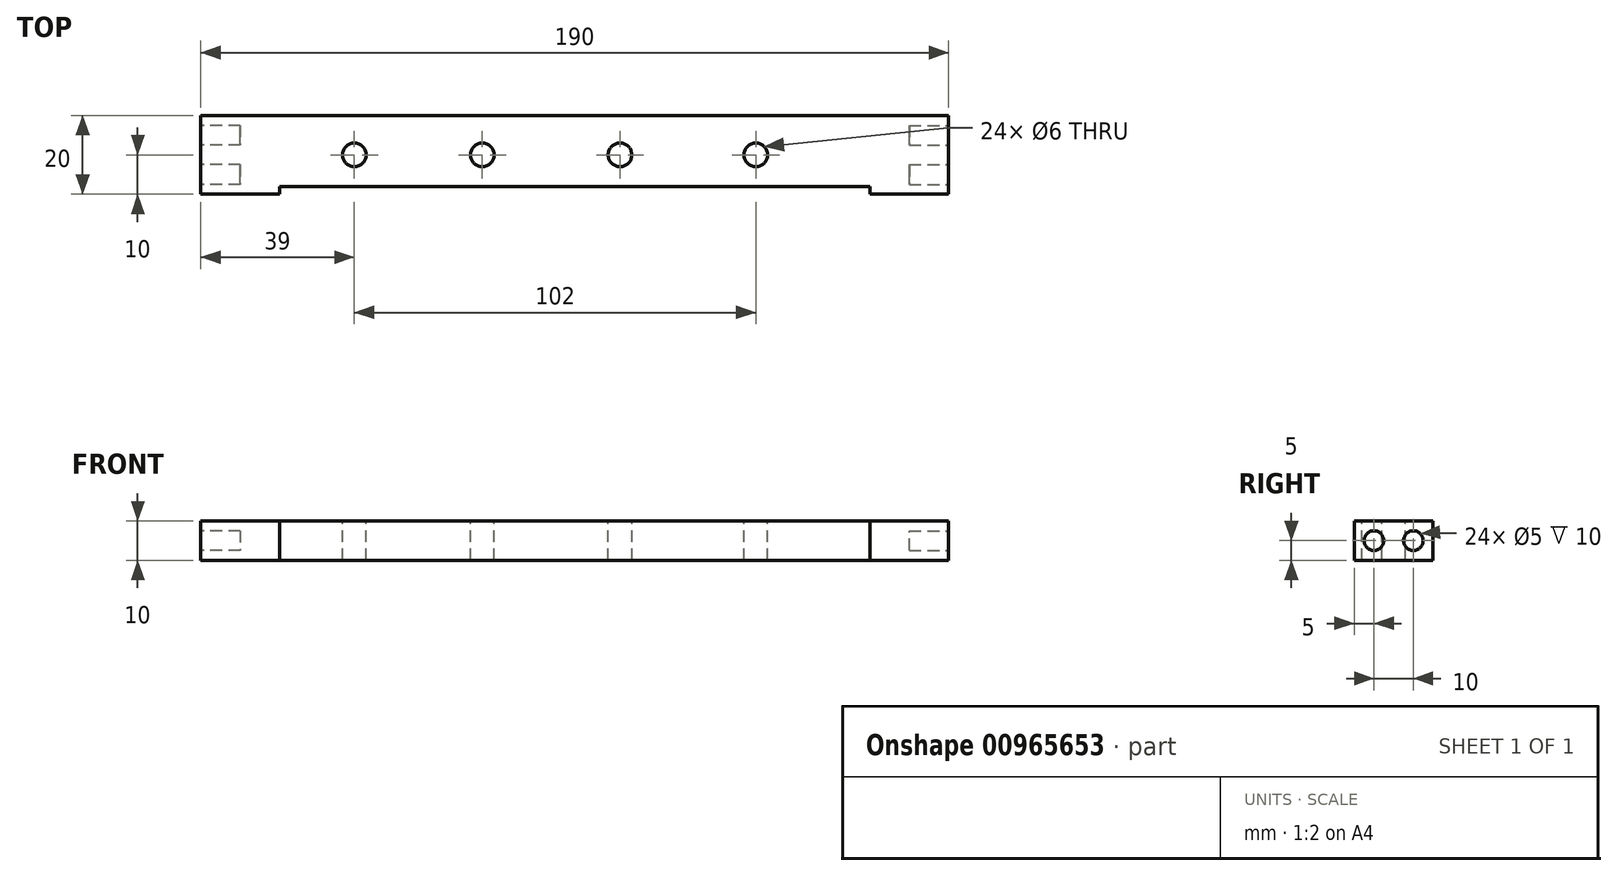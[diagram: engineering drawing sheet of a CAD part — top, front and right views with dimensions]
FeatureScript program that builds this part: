
annotation { "Feature Type Name" : "Feature", "Feature Type Description" : "" }
export const myFeature = defineFeature(function(context is Context, id is Id, definition is map)
    precondition{}
    {
        {
            var Q0;
            Q0=qCreatedBy(makeId("Front.planeOp"),FACE);
            var sketch = newSketch(context, id + "F0", { "sketchPlane" : qUnion([Q0])});
            skLineSegment(sketch, "E0.bottom", {"start": v(95, -5) * mm, "end": v(-95, -5) * mm});
            skLineSegment(sketch, "E0.top", {"start": v(95, 5) * mm, "end": v(-95, 5) * mm});
            skLineSegment(sketch, "E0.left", {"start": v(95, -5) * mm, "end": v(95, 5) * mm});
            skLineSegment(sketch, "E0.right", {"start": v(-95, -5) * mm, "end": v(-95, 5) * mm});
            skPoint(sketch, "E0.middle", {"position": v(0, 0) * mm});
            skSolve(sketch);
        }
        {
            var Q0;
            Q0=makeQuery(id+"F0.imprint","IMPRINT",FACE,{"disambiguationData":[TD([[makeQuery(id+"F0.imprint","IMPRINT",EDGE,{"derivedFrom":sQuery(id+"F0.wireOp",EDGE,"E0.bottom")}),-1.0]])]});
            extrude(context, id + "F1", {"entities" : qUnion([Q0]), "depth" : 20 * mm, "offsetDistance" : 25 * mm});
        }
        {
            var Q0;
            Q0=makeQuery(id+"F1.opExtrude","SWEPT_FACE",FACE,{"disambiguationData":[OSD([sQuery(id+"F0.wireOp",EDGE,"E0.top")])]});
            var sketch = newSketch(context, id + "F2", { "sketchPlane" : qUnion([Q0])});
            skCircle(sketch, "E1", {"center": v(-56, -10) * mm, "radius": 3 * mm});
            skCircle(sketch, "E2", {"center": v(-23.5, -10) * mm, "radius": 3 * mm});
            skCircle(sketch, "E3", {"center": v(11.5, -10) * mm, "radius": 3 * mm});
            skCircle(sketch, "E4", {"center": v(46, -10) * mm, "radius": 3 * mm});
            skLineSegment(sketch, "E5.right", {"start": v(-75, -20.5) * mm, "end": v(-75, -18) * mm});
            skLineSegment(sketch, "E6.bottom", {"start": v(-75, -18) * mm, "end": v(75, -18) * mm});
            skLineSegment(sketch, "E6.top", {"start": v(-75, -20) * mm, "end": v(75, -20) * mm});
            skLineSegment(sketch, "E6.left", {"start": v(-75, -18) * mm, "end": v(-75, -20) * mm});
            skLineSegment(sketch, "E6.right", {"start": v(75, -18) * mm, "end": v(75, -20) * mm});
            skLineSegment(sketch, "E7.left", {"start": v(75, -18) * mm, "end": v(75, -20.5) * mm});
            skLineSegment(sketch, "E8.top", {"start": v(-75, 0) * mm, "end": v(75, 0) * mm});
            skSolve(sketch);
        }
        {
            var Q0;
            Q0 = qSketchRegion(id + "F2", true);
            extrude(context, id + "F3", {"entities" : qUnion([Q0]), "operationType" : NewBodyOperationType.REMOVE, "oppositeDirection" : true, "depth" : 10 * mm, "offsetDistance" : 25 * mm});
        }
        {
            var Q0;
            Q0=makeQuery(id+"F1.opExtrude","SWEPT_FACE",FACE,{"disambiguationData":[OSD([sQuery(id+"F0.wireOp",EDGE,"E0.right")])]});
            var sketch = newSketch(context, id + "F4", { "sketchPlane" : qUnion([Q0])});
            skCircle(sketch, "E9", {"center": v(5, 0) * mm, "radius": 2.5 * mm});
            skCircle(sketch, "E10", {"center": v(15, 0) * mm, "radius": 2.5 * mm});
            skSolve(sketch);
        }
        {
            var Q0;
            Q0 = qSketchRegion(id + "F4", true);
            extrude(context, id + "F5", {"entities" : qUnion([Q0]), "operationType" : NewBodyOperationType.REMOVE, "oppositeDirection" : true, "depth" : 10 * mm, "offsetDistance" : 25 * mm});
        }
        {
            var Q0;
            Q0=makeQuery(id+"F1.opExtrude","SWEPT_FACE",FACE,{"disambiguationData":[OSD([sQuery(id+"F0.wireOp",EDGE,"E0.left")])]});
            var sketch = newSketch(context, id + "F6", { "sketchPlane" : qUnion([Q0])});
            skCircle(sketch, "E11", {"center": v(-5, 0) * mm, "radius": 2.5 * mm});
            skCircle(sketch, "E12", {"center": v(-15, 0) * mm, "radius": 2.5 * mm});
            skSolve(sketch);
        }
        {
            var Q0;
            Q0 = qSketchRegion(id + "F6", true);
            extrude(context, id + "F7", {"entities" : qUnion([Q0]), "operationType" : NewBodyOperationType.REMOVE, "oppositeDirection" : true, "depth" : 10 * mm, "offsetDistance" : 25 * mm});
        }
    });
